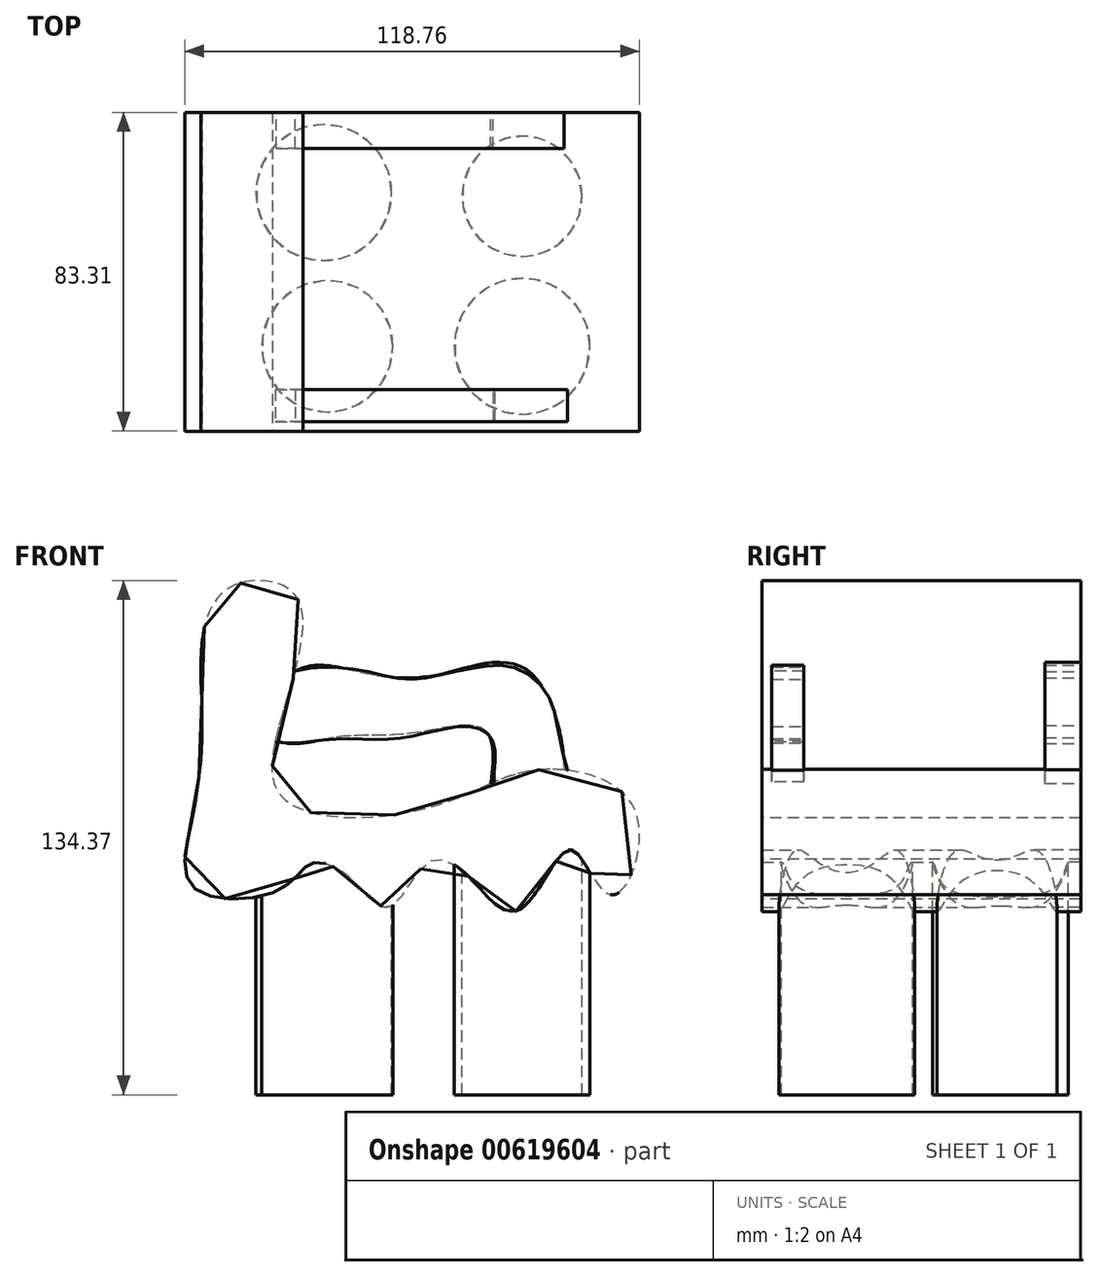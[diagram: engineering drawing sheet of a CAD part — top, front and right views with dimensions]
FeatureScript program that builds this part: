
annotation { "Feature Type Name" : "Feature", "Feature Type Description" : "" }
export const myFeature = defineFeature(function(context is Context, id is Id, definition is map)
    precondition{}
    {
        {
            var Q0;
            Q0=qCreatedBy(makeId("Front.planeOp"),FACE);
            var sketch = newSketch(context, id + "F0", { "sketchPlane" : qUnion([Q0])});
            skFitSpline(sketch, "E0", {"points": [v(-48.22, 56.24) * mm, v(-48.85, 34.24) * mm, v(-51.05, 7.85) * mm, v(-51.05, -11.94) * mm, v(-28.12, -12.25) * mm, v(-20.58, -5.65) * mm, v(-10.52, -9.11) * mm, v(0, -16.96) * mm, v(10.21, -5.34) * mm, v(20.58, -8.8) * mm, v(32.52, -18.22) * mm, v(43.2, -5.65) * mm, v(48.54, -2.51) * mm, v(58.28, -13.82) * mm, v(64.56, 7.54) * mm, v(39.43, 18.85) * mm, v(18.38, 11.62) * mm, v(-8.33, 6.28) * mm, v(-29.06, 13.2) * mm, v(-25.92, 39.58) * mm, v(-24.66, 64.72) * mm, v(-40.06, 67.23) * mm, v(-48.22, 56.24) * mm]});
            skSolve(sketch);
        }
        {
            var Q0;
            Q0=makeQuery(id+"F0.imprint","IMPRINT",FACE,{"disambiguationData":[TD([[makeQuery(id+"F0.imprint","IMPRINT",EDGE,{"derivedFrom":sQuery(id+"F0.wireOp",EDGE,"E0")}),1.0]])]});
            extrude(context, id + "F1", {"entities" : qUnion([Q0]), "depth" : 83.31 * mm, "offsetDistance" : 25.4 * mm});
        }
        {
            var Q0;
            Q0=qCreatedBy(makeId("Top.planeOp"),FACE);
            var sketch = newSketch(context, id + "F2", { "sketchPlane" : qUnion([Q0])});
            skCircle(sketch, "E1", {"center": v(34.77, -21.94) * mm, "radius": 15.68 * mm});
            skCircle(sketch, "E2", {"center": v(-17.04, -21) * mm, "radius": 17.74 * mm});
            skCircle(sketch, "E3", {"center": v(34.77, -61.14) * mm, "radius": 17.74 * mm});
            skCircle(sketch, "E4", {"center": v(-16.1, -61.14) * mm, "radius": 17.14 * mm});
            skSolve(sketch);
        }
        {
            var Q0;
            Q0 = qSketchRegion(id + "F2", true);
            extrude(context, id + "F3", {"entities" : qUnion([Q0]), "operationType" : NewBodyOperationType.ADD, "oppositeDirection" : true, "depth" : 66.04 * mm, "offsetDistance" : 25.4 * mm});
        }
        {
            var Q0;
            Q0=makeQuery(id+"F1.opExtrude","CAP_FACE",FACE,{"disambiguationData":[OSD([sQuery(id+"F0.wireOp",EDGE,"E0")])],"isStart":false});
            cPlane(context, id + "F4", {"entities" : qUnion([Q0]), "cplaneType" : CPlaneType.OFFSET, "offset" : 2.54 * mm, "oppositeDirection" : true, "width" : 152.4 * mm, "height" : 152.4 * mm});
        }
        {
            var Q0;
            Q0=qCreatedBy(makeId("Front.planeOp"),FACE);
            var sketch = newSketch(context, id + "F5", { "sketchPlane" : qUnion([Q0])});
            skFitSpline(sketch, "E5", {"points": [v(-25.26, 44) * mm, v(-5.47, 44) * mm, v(14.32, 44) * mm, v(37.24, 44) * mm, v(42.45, 5.47) * mm, v(27.86, 5.47) * mm, v(26.82, 16.93) * mm, v(24.74, 29.43) * mm, v(5.99, 28.38) * mm, v(-13.8, 27.34) * mm, v(-29.43, 27.34) * mm, v(-25.26, 44) * mm]});
            skSolve(sketch);
        }
        {
            var Q0;
            Q0 = qSketchRegion(id + "F5", true);
            extrude(context, id + "F6", {"entities" : qUnion([Q0]), "operationType" : NewBodyOperationType.ADD, "depth" : 9.4 * mm, "offsetDistance" : 25.4 * mm});
        }
        {
            var Q0;
            Q0=qCreatedBy(id+"F4.planeOp",FACE);
            var sketch = newSketch(context, id + "F7", { "sketchPlane" : qUnion([Q0])});
            skFitSpline(sketch, "E6", {"points": [v(-35.11, 38.34) * mm, v(-24.7, 44.59) * mm, v(-15.32, 45.63) * mm, v(-5.95, 44.59) * mm, v(4.47, 42.5) * mm, v(12.8, 43.54) * mm, v(23.22, 45.63) * mm, v(32.6, 45.63) * mm, v(40.92, 39.38) * mm, v(44.05, 30) * mm, v(46.13, 20.63) * mm, v(46.13, 6.04) * mm, v(31.55, 0) * mm, v(28.42, 10.21) * mm, v(27.38, 16.46) * mm, v(27.38, 25.84) * mm, v(22.17, 30) * mm, v(11.76, 28.96) * mm, v(0, 26.88) * mm, v(-14.28, 26.88) * mm, v(-26.78, 25.84) * mm, v(-36.16, 27.92) * mm], "startDerivative": vector(201.37, 147.03) * mm, "endDerivative": vector(-198.42, 64.1) * mm});
            skFitSpline(sketch, "E7", {"points": [v(-36.16, 27.92) * mm, v(-35.11, 38.34) * mm], "startDerivative": vector(1.04, 10.42) * mm, "endDerivative": vector(1.04, 10.42) * mm});
            skSolve(sketch);
        }
        {
            var Q0;
            Q0=makeQuery(id+"F7.imprint","IMPRINT",FACE,{"disambiguationData":[TD([[makeQuery(id+"F7.imprint","IMPRINT",EDGE,{"derivedFrom":sQuery(id+"F7.wireOp",EDGE,"E6")}),-1.0]])]});
            extrude(context, id + "F8", {"entities" : qUnion([Q0]), "operationType" : NewBodyOperationType.ADD, "oppositeDirection" : true, "depth" : 8.38 * mm, "offsetDistance" : 25.4 * mm});
        }
    });
